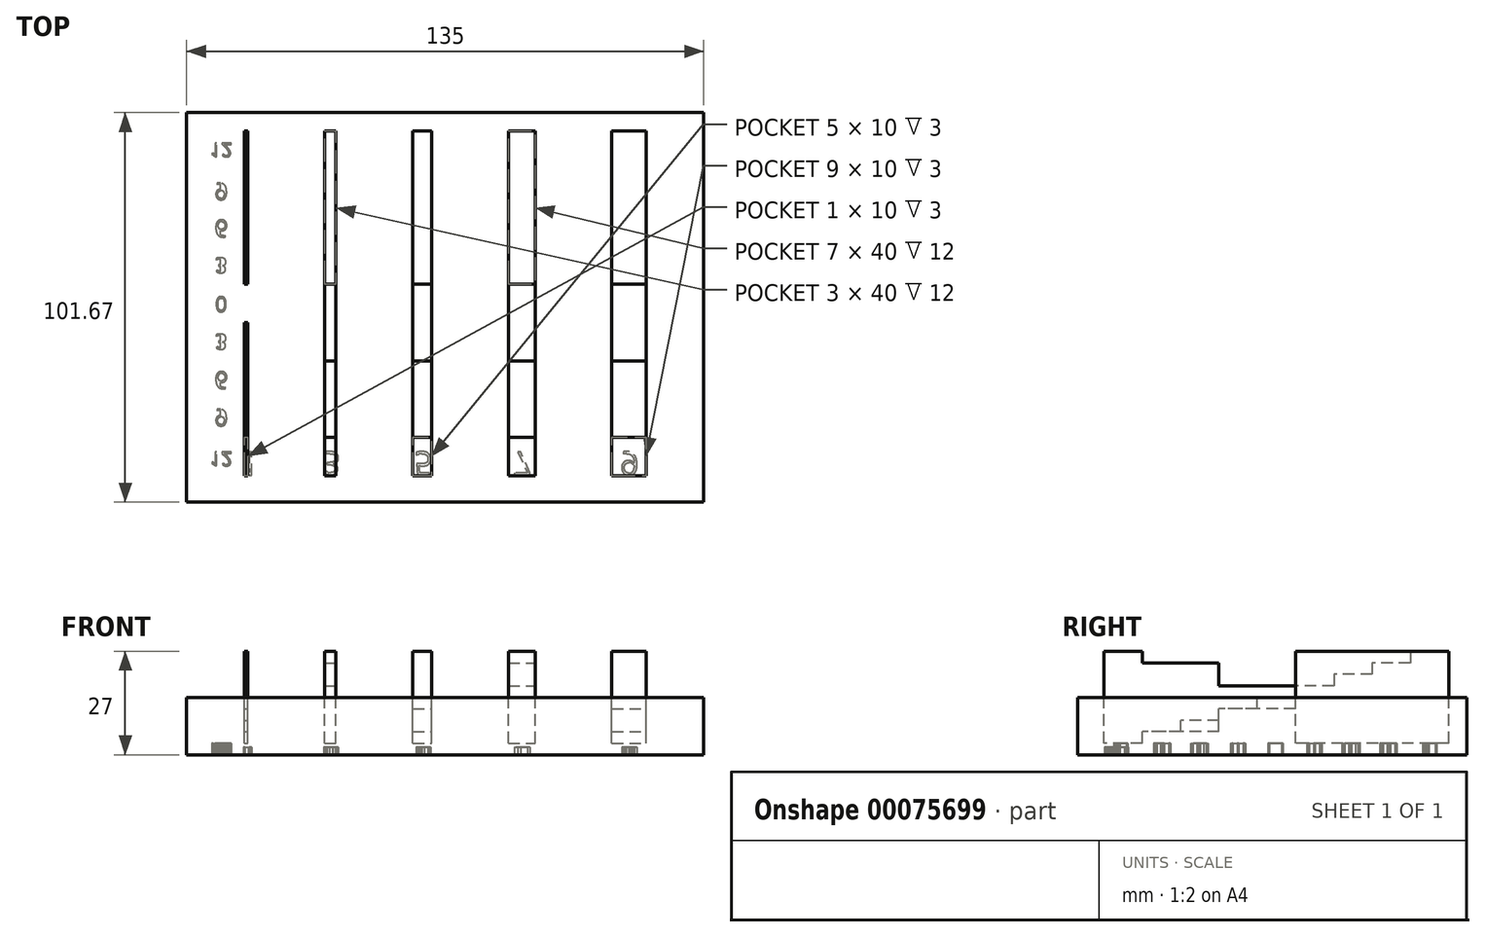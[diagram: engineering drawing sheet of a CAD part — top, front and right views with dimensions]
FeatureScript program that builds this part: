
annotation { "Feature Type Name" : "Feature", "Feature Type Description" : "" }
export const myFeature = defineFeature(function(context is Context, id is Id, definition is map)
    precondition{}
    {
        {
            var Q0;
            Q0=qCreatedBy(makeId("Top.planeOp"),FACE);
            var sketch = newSketch(context, id + "F0", { "sketchPlane" : qUnion([Q0])});
            skLineSegment(sketch, "E0.bottom", {"start": v(-38.42, 41.06) * mm, "end": v(-37.42, 41.06) * mm});
            skLineSegment(sketch, "E0.top", {"start": v(-38.42, 31.06) * mm, "end": v(-37.42, 31.06) * mm});
            skLineSegment(sketch, "E0.left", {"start": v(-38.42, 41.06) * mm, "end": v(-38.42, 31.06) * mm});
            skLineSegment(sketch, "E0.right", {"start": v(-37.42, 41.06) * mm, "end": v(-37.42, 31.06) * mm});
            skLineSegment(sketch, "E1.top", {"start": v(-38.42, 21.06) * mm, "end": v(-37.42, 21.06) * mm});
            skLineSegment(sketch, "E1.left", {"start": v(-38.42, 31.06) * mm, "end": v(-38.42, 21.06) * mm});
            skLineSegment(sketch, "E1.right", {"start": v(-37.42, 31.06) * mm, "end": v(-37.42, 21.06) * mm});
            skLineSegment(sketch, "E2.top", {"start": v(-38.42, 11.06) * mm, "end": v(-37.42, 11.06) * mm});
            skLineSegment(sketch, "E2.left", {"start": v(-38.42, 21.06) * mm, "end": v(-38.42, 11.06) * mm});
            skLineSegment(sketch, "E2.right", {"start": v(-37.42, 21.06) * mm, "end": v(-37.42, 11.06) * mm});
            skLineSegment(sketch, "E3.top", {"start": v(-38.42, 1.06) * mm, "end": v(-37.42, 1.06) * mm});
            skLineSegment(sketch, "E3.left", {"start": v(-38.42, 11.06) * mm, "end": v(-38.42, 1.06) * mm});
            skLineSegment(sketch, "E3.right", {"start": v(-37.42, 11.06) * mm, "end": v(-37.42, 1.06) * mm});
            skLineSegment(sketch, "E4.top", {"start": v(-38.42, -8.94) * mm, "end": v(-37.42, -8.94) * mm});
            skLineSegment(sketch, "E4.left", {"start": v(-38.42, 1.06) * mm, "end": v(-38.42, -8.94) * mm});
            skLineSegment(sketch, "E4.right", {"start": v(-37.42, 1.06) * mm, "end": v(-37.42, -8.94) * mm});
            skLineSegment(sketch, "E5.top", {"start": v(-38.42, -18.94) * mm, "end": v(-37.42, -18.94) * mm});
            skLineSegment(sketch, "E5.left", {"start": v(-38.42, -8.94) * mm, "end": v(-38.42, -18.94) * mm});
            skLineSegment(sketch, "E5.right", {"start": v(-37.42, -8.94) * mm, "end": v(-37.42, -18.94) * mm});
            skLineSegment(sketch, "E6.top", {"start": v(-38.42, -28.94) * mm, "end": v(-37.42, -28.94) * mm});
            skLineSegment(sketch, "E6.left", {"start": v(-38.42, -18.94) * mm, "end": v(-38.42, -28.94) * mm});
            skLineSegment(sketch, "E6.right", {"start": v(-37.42, -18.94) * mm, "end": v(-37.42, -28.94) * mm});
            skLineSegment(sketch, "E7.top", {"start": v(-38.42, -38.94) * mm, "end": v(-37.42, -38.94) * mm});
            skLineSegment(sketch, "E7.left", {"start": v(-38.42, -28.94) * mm, "end": v(-38.42, -38.94) * mm});
            skLineSegment(sketch, "E7.right", {"start": v(-37.42, -28.94) * mm, "end": v(-37.42, -38.94) * mm});
            skLineSegment(sketch, "E8.top", {"start": v(-17.42, -18.94) * mm, "end": v(-14.42, -18.94) * mm});
            skLineSegment(sketch, "E9.bottom", {"start": v(-17.42, -38.94) * mm, "end": v(-14.42, -38.94) * mm});
            skLineSegment(sketch, "E10.right", {"start": v(-14.42, -18.94) * mm, "end": v(-14.42, -28.94) * mm});
            skLineSegment(sketch, "E11.left", {"start": v(-17.42, 21.06) * mm, "end": v(-17.42, 11.06) * mm});
            skLineSegment(sketch, "E10.left", {"start": v(-17.42, -18.94) * mm, "end": v(-17.42, -28.94) * mm});
            skLineSegment(sketch, "E12.bottom", {"start": v(-17.42, 1.06) * mm, "end": v(-14.42, 1.06) * mm});
            skLineSegment(sketch, "E12.right", {"start": v(-14.42, 1.06) * mm, "end": v(-14.42, -8.94) * mm});
            skLineSegment(sketch, "E13.left", {"start": v(-17.42, 11.06) * mm, "end": v(-17.42, 1.06) * mm});
            skLineSegment(sketch, "E13.right", {"start": v(-14.42, 11.06) * mm, "end": v(-14.42, 1.06) * mm});
            skLineSegment(sketch, "E14.left", {"start": v(-17.42, 41.06) * mm, "end": v(-17.42, 31.06) * mm});
            skLineSegment(sketch, "E15.left", {"start": v(-17.42, 31.06) * mm, "end": v(-17.42, 21.06) * mm});
            skLineSegment(sketch, "E15.right", {"start": v(-14.42, 31.06) * mm, "end": v(-14.42, 21.06) * mm});
            skLineSegment(sketch, "E11.right", {"start": v(-14.42, 21.06) * mm, "end": v(-14.42, 11.06) * mm});
            skLineSegment(sketch, "E8.right", {"start": v(-14.42, -8.94) * mm, "end": v(-14.42, -18.94) * mm});
            skLineSegment(sketch, "E16.left", {"start": v(-17.42, -28.94) * mm, "end": v(-17.42, -38.94) * mm});
            skLineSegment(sketch, "E8.left", {"start": v(-17.42, -8.94) * mm, "end": v(-17.42, -18.94) * mm});
            skLineSegment(sketch, "E12.left", {"start": v(-17.42, 1.06) * mm, "end": v(-17.42, -8.94) * mm});
            skLineSegment(sketch, "E16.right", {"start": v(-14.42, -28.94) * mm, "end": v(-14.42, -38.94) * mm});
            skLineSegment(sketch, "E14.bottom", {"start": v(-17.42, 41.06) * mm, "end": v(-14.42, 41.06) * mm});
            skLineSegment(sketch, "E14.right", {"start": v(-14.42, 41.06) * mm, "end": v(-14.42, 31.06) * mm});
            skLineSegment(sketch, "E17.top", {"start": v(5.58, -18.94) * mm, "end": v(10.58, -18.94) * mm});
            skLineSegment(sketch, "E18.bottom", {"start": v(5.58, -38.94) * mm, "end": v(10.58, -38.94) * mm});
            skLineSegment(sketch, "E19.right", {"start": v(10.58, -18.94) * mm, "end": v(10.58, -28.94) * mm});
            skLineSegment(sketch, "E20.left", {"start": v(5.58, 21.06) * mm, "end": v(5.58, 11.06) * mm});
            skLineSegment(sketch, "E19.left", {"start": v(5.58, -18.94) * mm, "end": v(5.58, -28.94) * mm});
            skLineSegment(sketch, "E21.bottom", {"start": v(5.58, 1.06) * mm, "end": v(10.58, 1.06) * mm});
            skLineSegment(sketch, "E21.right", {"start": v(10.58, 1.06) * mm, "end": v(10.58, -8.94) * mm});
            skLineSegment(sketch, "E22.left", {"start": v(5.58, 11.06) * mm, "end": v(5.58, 1.06) * mm});
            skLineSegment(sketch, "E22.right", {"start": v(10.58, 11.06) * mm, "end": v(10.58, 1.06) * mm});
            skLineSegment(sketch, "E23.left", {"start": v(5.58, 41.06) * mm, "end": v(5.58, 31.06) * mm});
            skLineSegment(sketch, "E24.left", {"start": v(5.58, 31.06) * mm, "end": v(5.58, 21.06) * mm});
            skLineSegment(sketch, "E24.right", {"start": v(10.58, 31.06) * mm, "end": v(10.58, 21.06) * mm});
            skLineSegment(sketch, "E20.right", {"start": v(10.58, 21.06) * mm, "end": v(10.58, 11.06) * mm});
            skLineSegment(sketch, "E17.right", {"start": v(10.58, -8.94) * mm, "end": v(10.58, -18.94) * mm});
            skLineSegment(sketch, "E25.left", {"start": v(5.58, -28.94) * mm, "end": v(5.58, -38.94) * mm});
            skLineSegment(sketch, "E17.left", {"start": v(5.58, -8.94) * mm, "end": v(5.58, -18.94) * mm});
            skLineSegment(sketch, "E21.left", {"start": v(5.58, 1.06) * mm, "end": v(5.58, -8.94) * mm});
            skLineSegment(sketch, "E25.right", {"start": v(10.58, -28.94) * mm, "end": v(10.58, -38.94) * mm});
            skLineSegment(sketch, "E23.bottom", {"start": v(5.58, 41.06) * mm, "end": v(10.58, 41.06) * mm});
            skLineSegment(sketch, "E23.right", {"start": v(10.58, 41.06) * mm, "end": v(10.58, 31.06) * mm});
            skLineSegment(sketch, "E26.top", {"start": v(30.58, -18.94) * mm, "end": v(37.58, -18.94) * mm});
            skLineSegment(sketch, "E27.bottom", {"start": v(30.58, -38.94) * mm, "end": v(37.58, -38.94) * mm});
            skLineSegment(sketch, "E28.right", {"start": v(37.58, -18.94) * mm, "end": v(37.58, -28.94) * mm});
            skLineSegment(sketch, "E29.left", {"start": v(30.58, 21.06) * mm, "end": v(30.58, 11.06) * mm});
            skLineSegment(sketch, "E28.left", {"start": v(30.58, -18.94) * mm, "end": v(30.58, -28.94) * mm});
            skLineSegment(sketch, "E30.bottom", {"start": v(30.58, 1.06) * mm, "end": v(37.58, 1.06) * mm});
            skLineSegment(sketch, "E30.right", {"start": v(37.58, 1.06) * mm, "end": v(37.58, -8.94) * mm});
            skLineSegment(sketch, "E31.left", {"start": v(30.58, 11.06) * mm, "end": v(30.58, 1.06) * mm});
            skLineSegment(sketch, "E31.right", {"start": v(37.58, 11.06) * mm, "end": v(37.58, 1.06) * mm});
            skLineSegment(sketch, "E32.left", {"start": v(30.58, 41.06) * mm, "end": v(30.58, 31.06) * mm});
            skLineSegment(sketch, "E33.left", {"start": v(30.58, 31.06) * mm, "end": v(30.58, 21.06) * mm});
            skLineSegment(sketch, "E33.right", {"start": v(37.58, 31.06) * mm, "end": v(37.58, 21.06) * mm});
            skLineSegment(sketch, "E29.right", {"start": v(37.58, 21.06) * mm, "end": v(37.58, 11.06) * mm});
            skLineSegment(sketch, "E26.right", {"start": v(37.58, -8.94) * mm, "end": v(37.58, -18.94) * mm});
            skLineSegment(sketch, "E34.left", {"start": v(30.58, -28.94) * mm, "end": v(30.58, -38.94) * mm});
            skLineSegment(sketch, "E26.left", {"start": v(30.58, -8.94) * mm, "end": v(30.58, -18.94) * mm});
            skLineSegment(sketch, "E30.left", {"start": v(30.58, 1.06) * mm, "end": v(30.58, -8.94) * mm});
            skLineSegment(sketch, "E34.right", {"start": v(37.58, -28.94) * mm, "end": v(37.58, -38.94) * mm});
            skLineSegment(sketch, "E32.bottom", {"start": v(30.58, 41.06) * mm, "end": v(37.58, 41.06) * mm});
            skLineSegment(sketch, "E32.right", {"start": v(37.58, 41.06) * mm, "end": v(37.58, 31.06) * mm});
            skLineSegment(sketch, "E35.top", {"start": v(57.58, -18.94) * mm, "end": v(66.58, -18.94) * mm});
            skLineSegment(sketch, "E36.bottom", {"start": v(57.58, -38.94) * mm, "end": v(66.58, -38.94) * mm});
            skLineSegment(sketch, "E37.right", {"start": v(66.58, -18.94) * mm, "end": v(66.58, -28.94) * mm});
            skLineSegment(sketch, "E38.left", {"start": v(57.58, 21.06) * mm, "end": v(57.58, 11.06) * mm});
            skLineSegment(sketch, "E37.left", {"start": v(57.58, -18.94) * mm, "end": v(57.58, -28.94) * mm});
            skLineSegment(sketch, "E39.bottom", {"start": v(57.58, 1.06) * mm, "end": v(66.58, 1.06) * mm});
            skLineSegment(sketch, "E39.right", {"start": v(66.58, 1.06) * mm, "end": v(66.58, -8.94) * mm});
            skLineSegment(sketch, "E40.left", {"start": v(57.58, 11.06) * mm, "end": v(57.58, 1.06) * mm});
            skLineSegment(sketch, "E40.right", {"start": v(66.58, 11.06) * mm, "end": v(66.58, 1.06) * mm});
            skLineSegment(sketch, "E41.left", {"start": v(57.58, 41.06) * mm, "end": v(57.58, 31.06) * mm});
            skLineSegment(sketch, "E42.left", {"start": v(57.58, 31.06) * mm, "end": v(57.58, 21.06) * mm});
            skLineSegment(sketch, "E42.right", {"start": v(66.58, 31.06) * mm, "end": v(66.58, 21.06) * mm});
            skLineSegment(sketch, "E38.right", {"start": v(66.58, 21.06) * mm, "end": v(66.58, 11.06) * mm});
            skLineSegment(sketch, "E35.right", {"start": v(66.58, -8.94) * mm, "end": v(66.58, -18.94) * mm});
            skLineSegment(sketch, "E43.left", {"start": v(57.58, -28.94) * mm, "end": v(57.58, -38.94) * mm});
            skLineSegment(sketch, "E35.left", {"start": v(57.58, -8.94) * mm, "end": v(57.58, -18.94) * mm});
            skLineSegment(sketch, "E39.left", {"start": v(57.58, 1.06) * mm, "end": v(57.58, -8.94) * mm});
            skLineSegment(sketch, "E43.right", {"start": v(66.58, -28.94) * mm, "end": v(66.58, -38.94) * mm});
            skLineSegment(sketch, "E41.bottom", {"start": v(57.58, 41.06) * mm, "end": v(66.58, 41.06) * mm});
            skLineSegment(sketch, "E41.right", {"start": v(66.58, 41.06) * mm, "end": v(66.58, 31.06) * mm});
            skLineSegment(sketch, "E44.bottom", {"start": v(-53.42, 45.85) * mm, "end": v(81.58, 45.85) * mm});
            skLineSegment(sketch, "E44.top", {"start": v(-53.42, -55.82) * mm, "end": v(81.58, -55.82) * mm});
            skLineSegment(sketch, "E44.left", {"start": v(-53.42, 45.85) * mm, "end": v(-53.42, -55.82) * mm});
            skLineSegment(sketch, "E44.right", {"start": v(81.58, 45.85) * mm, "end": v(81.58, -55.82) * mm});
            skLineSegment(sketch, "E45", {"start": v(-14.42, 1.06) * mm, "end": v(5.58, 1.06) * mm});
            skLineSegment(sketch, "E46", {"start": v(10.58, 1.06) * mm, "end": v(30.58, 1.06) * mm});
            skLineSegment(sketch, "E47", {"start": v(37.58, 1.06) * mm, "end": v(57.58, 1.06) * mm});
            skLineSegment(sketch, "E48", {"start": v(66.58, 1.06) * mm, "end": v(81.58, 1.06) * mm});
            skLineSegment(sketch, "E49", {"start": v(-38.42, 1.06) * mm, "end": v(-53.42, 1.06) * mm});
            skLineSegment(sketch, "E50", {"start": v(-37.42, 1.06) * mm, "end": v(-17.42, 1.06) * mm});
            skLineSegment(sketch, "E51", {"start": v(-38.42, -38.94) * mm, "end": v(-38.42, -48.94) * mm});
            skLineSegment(sketch, "E52", {"start": v(-38.42, -48.94) * mm, "end": v(-37.42, -48.94) * mm});
            skLineSegment(sketch, "E53", {"start": v(-37.42, -48.94) * mm, "end": v(-37.42, -38.94) * mm});
            skLineSegment(sketch, "E54", {"start": v(-17.42, -38.94) * mm, "end": v(-17.42, -48.94) * mm});
            skLineSegment(sketch, "E55", {"start": v(-17.42, -48.94) * mm, "end": v(-14.42, -48.94) * mm});
            skLineSegment(sketch, "E56", {"start": v(-14.42, -48.94) * mm, "end": v(-14.42, -38.94) * mm});
            skLineSegment(sketch, "E57", {"start": v(5.58, -38.94) * mm, "end": v(5.58, -48.94) * mm});
            skLineSegment(sketch, "E58", {"start": v(5.58, -48.94) * mm, "end": v(10.58, -48.94) * mm});
            skLineSegment(sketch, "E59", {"start": v(10.58, -48.94) * mm, "end": v(10.58, -38.94) * mm});
            skLineSegment(sketch, "E60", {"start": v(30.58, -38.94) * mm, "end": v(30.58, -48.94) * mm});
            skLineSegment(sketch, "E61", {"start": v(30.58, -48.94) * mm, "end": v(37.58, -48.94) * mm});
            skLineSegment(sketch, "E62", {"start": v(37.58, -48.94) * mm, "end": v(37.58, -38.94) * mm});
            skLineSegment(sketch, "E63", {"start": v(57.58, -38.94) * mm, "end": v(57.58, -48.94) * mm});
            skLineSegment(sketch, "E64", {"start": v(57.58, -48.94) * mm, "end": v(66.58, -48.94) * mm});
            skLineSegment(sketch, "E65", {"start": v(66.58, -48.94) * mm, "end": v(66.58, -38.94) * mm});
            skSolve(sketch);
        }
        {
            var Q0;
            Q0=makeQuery(id+"F0.imprint","IMPRINT",FACE,{"disambiguationData":[TD([[makeQuery(id+"F0.imprint","IMPRINT",EDGE,{"derivedFrom":sQuery(id+"F0.wireOp",EDGE,"E27.right")}),-1.0]])]});
            var Q1;
            Q1=makeQuery(id+"F0.imprint","IMPRINT",FACE,{"disambiguationData":[TD([[makeQuery(id+"F0.imprint","IMPRINT",EDGE,{"derivedFrom":sQuery(id+"F0.wireOp",EDGE,"E9.right")}),-1.0]])]});
            var Q2;
            Q2=makeQuery(id+"F0.imprint","IMPRINT",FACE,{"disambiguationData":[TD([[makeQuery(id+"F0.imprint","IMPRINT",EDGE,{"derivedFrom":sQuery(id+"F0.wireOp",EDGE,"E36.right")}),-1.0]])]});
            var Q3;
            Q3=makeQuery(id+"F0.imprint","IMPRINT",FACE,{"disambiguationData":[TD([[makeQuery(id+"F0.imprint","IMPRINT",EDGE,{"derivedFrom":sQuery(id+"F0.wireOp",EDGE,"E18.right")}),-1.0]])]});
            var Q4;
            Q4=makeQuery(id+"F0.imprint","IMPRINT",FACE,{"disambiguationData":[TD([[makeQuery(id+"F0.imprint","IMPRINT",EDGE,{"derivedFrom":sQuery(id+"F0.wireOp",EDGE,"E22.left")}),1.0]])]});
            var Q5;
            Q5=makeQuery(id+"F0.imprint","IMPRINT",FACE,{"disambiguationData":[TD([[makeQuery(id+"F0.imprint","IMPRINT",EDGE,{"derivedFrom":sQuery(id+"F0.wireOp",EDGE,"E40.left")}),1.0]])]});
            var Q6;
            Q6=makeQuery(id+"F0.imprint","IMPRINT",FACE,{"disambiguationData":[TD([[makeQuery(id+"F0.imprint","IMPRINT",EDGE,{"derivedFrom":sQuery(id+"F0.wireOp",EDGE,"E16.left")}),1.0]])]});
            var Q7;
            Q7=makeQuery(id+"F0.imprint","IMPRINT",FACE,{"disambiguationData":[TD([[makeQuery(id+"F0.imprint","IMPRINT",EDGE,{"derivedFrom":sQuery(id+"F0.wireOp",EDGE,"E19.right")}),-1.0]])]});
            var Q8;
            Q8=makeQuery(id+"F0.imprint","IMPRINT",FACE,{"disambiguationData":[TD([[makeQuery(id+"F0.imprint","IMPRINT",EDGE,{"derivedFrom":sQuery(id+"F0.wireOp",EDGE,"E37.right")}),-1.0]])]});
            var Q9;
            Q9=makeQuery(id+"F0.imprint","IMPRINT",FACE,{"disambiguationData":[TD([[makeQuery(id+"F0.imprint","IMPRINT",EDGE,{"derivedFrom":sQuery(id+"F0.wireOp",EDGE,"E38.left")}),1.0]])]});
            var Q10;
            {var subQ0=sQuery(id+"F0.wireOp",EDGE,"E20.left");Q10=makeQuery(id+"F0.imprint","IMPRINT",FACE,{"disambiguationData":[TD([[makeQuery(id+"F0.imprint","IMPRINT",EDGE,{"derivedFrom":subQ0}),1.0]])]});}
            var Q11;
            Q11=makeQuery(id+"F0.imprint","IMPRINT",FACE,{"disambiguationData":[TD([[makeQuery(id+"F0.imprint","IMPRINT",EDGE,{"derivedFrom":sQuery(id+"F0.wireOp",EDGE,"E39.right")}),-1.0]])]});
            var Q12;
            Q12=makeQuery(id+"F0.imprint","IMPRINT",FACE,{"disambiguationData":[TD([[makeQuery(id+"F0.imprint","IMPRINT",EDGE,{"derivedFrom":sQuery(id+"F0.wireOp",EDGE,"E21.right")}),-1.0]])]});
            var Q13;
            Q13=makeQuery(id+"F0.imprint","IMPRINT",FACE,{"disambiguationData":[TD([[makeQuery(id+"F0.imprint","IMPRINT",EDGE,{"derivedFrom":sQuery(id+"F0.wireOp",EDGE,"E10.right")}),-1.0]])]});
            var Q14;
            Q14=makeQuery(id+"F0.imprint","IMPRINT",FACE,{"disambiguationData":[TD([[makeQuery(id+"F0.imprint","IMPRINT",EDGE,{"derivedFrom":sQuery(id+"F0.wireOp",EDGE,"E28.right")}),-1.0]])]});
            var Q15;
            {var subQ0=sQuery(id+"F0.wireOp",EDGE,"E11.left");Q15=makeQuery(id+"F0.imprint","IMPRINT",FACE,{"disambiguationData":[TD([[makeQuery(id+"F0.imprint","IMPRINT",EDGE,{"derivedFrom":subQ0}),1.0]])]});}
            var Q16;
            Q16=makeQuery(id+"F0.imprint","IMPRINT",FACE,{"disambiguationData":[TD([[makeQuery(id+"F0.imprint","IMPRINT",EDGE,{"derivedFrom":sQuery(id+"F0.wireOp",EDGE,"E35.right")}),-1.0]])]});
            var Q17;
            Q17=makeQuery(id+"F0.imprint","IMPRINT",FACE,{"disambiguationData":[TD([[makeQuery(id+"F0.imprint","IMPRINT",EDGE,{"derivedFrom":sQuery(id+"F0.wireOp",EDGE,"E17.right")}),-1.0]])]});
            var Q18;
            {var subQ0=sQuery(id+"F0.wireOp",EDGE,"E29.left");Q18=makeQuery(id+"F0.imprint","IMPRINT",FACE,{"disambiguationData":[TD([[makeQuery(id+"F0.imprint","IMPRINT",EDGE,{"derivedFrom":subQ0}),1.0]])]});}
            var Q19;
            {var subQ0=sQuery(id+"F0.wireOp",EDGE,"E24.left");Q19=makeQuery(id+"F0.imprint","IMPRINT",FACE,{"disambiguationData":[TD([[makeQuery(id+"F0.imprint","IMPRINT",EDGE,{"derivedFrom":subQ0}),1.0]])]});}
            var Q20;
            Q20=makeQuery(id+"F0.imprint","IMPRINT",FACE,{"disambiguationData":[TD([[makeQuery(id+"F0.imprint","IMPRINT",EDGE,{"derivedFrom":sQuery(id+"F0.wireOp",EDGE,"E43.left")}),1.0]])]});
            var Q21;
            Q21=makeQuery(id+"F0.imprint","IMPRINT",FACE,{"disambiguationData":[TD([[makeQuery(id+"F0.imprint","IMPRINT",EDGE,{"derivedFrom":sQuery(id+"F0.wireOp",EDGE,"E25.left")}),1.0]])]});
            var Q22;
            Q22=makeQuery(id+"F0.imprint","IMPRINT",FACE,{"disambiguationData":[TD([[makeQuery(id+"F0.imprint","IMPRINT",EDGE,{"derivedFrom":sQuery(id+"F0.wireOp",EDGE,"E34.left")}),1.0]])]});
            var Q23;
            Q23=makeQuery(id+"F0.imprint","IMPRINT",FACE,{"disambiguationData":[TD([[makeQuery(id+"F0.imprint","IMPRINT",EDGE,{"derivedFrom":sQuery(id+"F0.wireOp",EDGE,"E12.right")}),-1.0]])]});
            var Q24;
            Q24=makeQuery(id+"F0.imprint","IMPRINT",FACE,{"disambiguationData":[TD([[makeQuery(id+"F0.imprint","IMPRINT",EDGE,{"derivedFrom":sQuery(id+"F0.wireOp",EDGE,"E30.right")}),-1.0]])]});
            var Q25;
            {var subQ0=sQuery(id+"F0.wireOp",EDGE,"E31.left");Q25=makeQuery(id+"F0.imprint","IMPRINT",FACE,{"disambiguationData":[TD([[makeQuery(id+"F0.imprint","IMPRINT",EDGE,{"derivedFrom":subQ0}),1.0]])]});}
            var Q26;
            {var subQ0=sQuery(id+"F0.wireOp",EDGE,"E13.left");Q26=makeQuery(id+"F0.imprint","IMPRINT",FACE,{"disambiguationData":[TD([[makeQuery(id+"F0.imprint","IMPRINT",EDGE,{"derivedFrom":subQ0}),1.0]])]});}
            var Q27;
            Q27=makeQuery(id+"F0.imprint","IMPRINT",FACE,{"disambiguationData":[TD([[makeQuery(id+"F0.imprint","IMPRINT",EDGE,{"derivedFrom":sQuery(id+"F0.wireOp",EDGE,"2a3499dd-0f45-481c-83e2-7a4d8ce4059a.right")}),-1.0]])]});
            var Q28;
            Q28=makeQuery(id+"F0.imprint","IMPRINT",FACE,{"disambiguationData":[TD([[makeQuery(id+"F0.imprint","IMPRINT",EDGE,{"derivedFrom":sQuery(id+"F0.wireOp",EDGE,"b8b1e6fe-e81b-4528-8c0a-a502875816c5.right")}),-1.0]])]});
            var Q29;
            Q29=makeQuery(id+"F0.imprint","IMPRINT",FACE,{"disambiguationData":[TD([[makeQuery(id+"F0.imprint","IMPRINT",EDGE,{"derivedFrom":sQuery(id+"F0.wireOp",EDGE,"E23.left")}),1.0]])]});
            var Q30;
            Q30=makeQuery(id+"F0.imprint","IMPRINT",FACE,{"disambiguationData":[TD([[makeQuery(id+"F0.imprint","IMPRINT",EDGE,{"derivedFrom":sQuery(id+"F0.wireOp",EDGE,"b7528009-93d2-41cc-b916-c0be01132167.right")}),-1.0]])]});
            var Q31;
            Q31=makeQuery(id+"F0.imprint","IMPRINT",FACE,{"disambiguationData":[TD([[makeQuery(id+"F0.imprint","IMPRINT",EDGE,{"derivedFrom":sQuery(id+"F0.wireOp",EDGE,"cfbb6618-f7cc-4c27-93e8-6fec4e00b0a7.right")}),-1.0]])]});
            var Q32;
            Q32=makeQuery(id+"F0.imprint","IMPRINT",FACE,{"disambiguationData":[TD([[makeQuery(id+"F0.imprint","IMPRINT",EDGE,{"derivedFrom":sQuery(id+"F0.wireOp",EDGE,"E33.left")}),1.0]])]});
            var Q33;
            Q33=makeQuery(id+"F0.imprint","IMPRINT",FACE,{"disambiguationData":[TD([[makeQuery(id+"F0.imprint","IMPRINT",EDGE,{"derivedFrom":sQuery(id+"F0.wireOp",EDGE,"E15.left")}),1.0]])]});
            var Q34;
            Q34=makeQuery(id+"F0.imprint","IMPRINT",FACE,{"disambiguationData":[TD([[makeQuery(id+"F0.imprint","IMPRINT",EDGE,{"derivedFrom":sQuery(id+"F0.wireOp",EDGE,"E26.right")}),-1.0]])]});
            var Q35;
            Q35=makeQuery(id+"F0.imprint","IMPRINT",FACE,{"disambiguationData":[TD([[makeQuery(id+"F0.imprint","IMPRINT",EDGE,{"derivedFrom":sQuery(id+"F0.wireOp",EDGE,"E8.right")}),-1.0]])]});
            var Q36;
            Q36=makeQuery(id+"F0.imprint","IMPRINT",FACE,{"disambiguationData":[TD([[makeQuery(id+"F0.imprint","IMPRINT",EDGE,{"derivedFrom":sQuery(id+"F0.wireOp",EDGE,"E42.left")}),1.0]])]});
            var Q37;
            Q37=makeQuery(id+"F0.imprint","IMPRINT",FACE,{"disambiguationData":[TD([[makeQuery(id+"F0.imprint","IMPRINT",EDGE,{"derivedFrom":sQuery(id+"F0.wireOp",EDGE,"E6.top")}),-1.0]])]});
            var Q38;
            Q38=makeQuery(id+"F0.imprint","IMPRINT",FACE,{"disambiguationData":[TD([[makeQuery(id+"F0.imprint","IMPRINT",EDGE,{"derivedFrom":sQuery(id+"F0.wireOp",EDGE,"E5.top")}),-1.0]])]});
            var Q39;
            Q39=makeQuery(id+"F0.imprint","IMPRINT",FACE,{"disambiguationData":[TD([[makeQuery(id+"F0.imprint","IMPRINT",EDGE,{"derivedFrom":sQuery(id+"F0.wireOp",EDGE,"E3.top")}),-1.0]])]});
            var Q40;
            Q40=makeQuery(id+"F0.imprint","IMPRINT",FACE,{"disambiguationData":[TD([[makeQuery(id+"F0.imprint","IMPRINT",EDGE,{"derivedFrom":sQuery(id+"F0.wireOp",EDGE,"E4.top")}),-1.0]])]});
            var Q41;
            Q41=makeQuery(id+"F0.imprint","IMPRINT",FACE,{"disambiguationData":[TD([[makeQuery(id+"F0.imprint","IMPRINT",EDGE,{"derivedFrom":sQuery(id+"F0.wireOp",EDGE,"7e96f1e9-1112-4445-a7ef-e244a0d670a8.bottom")}),-1.0]])]});
            var Q42;
            Q42=makeQuery(id+"F0.imprint","IMPRINT",FACE,{"disambiguationData":[TD([[makeQuery(id+"F0.imprint","IMPRINT",EDGE,{"derivedFrom":sQuery(id+"F0.wireOp",EDGE,"E14.left")}),1.0]])]});
            var Q43;
            Q43=makeQuery(id+"F0.imprint","IMPRINT",FACE,{"disambiguationData":[TD([[makeQuery(id+"F0.imprint","IMPRINT",EDGE,{"derivedFrom":sQuery(id+"F0.wireOp",EDGE,"E0.top")}),-1.0]])]});
            var Q44;
            {var subQ0=sQuery(id+"F0.wireOp",EDGE,"E2.left");Q44=makeQuery(id+"F0.imprint","IMPRINT",FACE,{"disambiguationData":[TD([[makeQuery(id+"F0.imprint","IMPRINT",EDGE,{"derivedFrom":subQ0}),1.0]])]});}
            var Q45;
            Q45=makeQuery(id+"F0.imprint","IMPRINT",FACE,{"disambiguationData":[TD([[makeQuery(id+"F0.imprint","IMPRINT",EDGE,{"derivedFrom":sQuery(id+"F0.wireOp",EDGE,"E2.top")}),-1.0]])]});
            var Q46;
            Q46=makeQuery(id+"F0.imprint","IMPRINT",FACE,{"disambiguationData":[TD([[makeQuery(id+"F0.imprint","IMPRINT",EDGE,{"derivedFrom":sQuery(id+"F0.wireOp",EDGE,"E0.bottom")}),-1.0]])]});
            var Q47;
            Q47=makeQuery(id+"F0.imprint","IMPRINT",FACE,{"disambiguationData":[TD([[makeQuery(id+"F0.imprint","IMPRINT",EDGE,{"derivedFrom":sQuery(id+"F0.wireOp",EDGE,"E41.left")}),1.0]])]});
            var Q48;
            Q48=makeQuery(id+"F0.imprint","IMPRINT",FACE,{"disambiguationData":[TD([[makeQuery(id+"F0.imprint","IMPRINT",EDGE,{"derivedFrom":sQuery(id+"F0.wireOp",EDGE,"E32.left")}),1.0]])]});
            var Q49;
            Q49=makeQuery(id+"F0.imprint","IMPRINT",FACE,{"disambiguationData":[TD([[makeQuery(id+"F0.imprint","IMPRINT",EDGE,{"derivedFrom":sQuery(id+"F0.wireOp",EDGE,"E0.bottom")}),1.0]])]});
            var Q50;
            Q50=makeQuery(id+"F0.imprint","IMPRINT",FACE,{"disambiguationData":[TD([[makeQuery(id+"F0.imprint","IMPRINT",EDGE,{"derivedFrom":sQuery(id+"F0.wireOp",EDGE,"E4.left")}),-1.0]])]});
            var Q51;
            Q51=makeQuery(id+"F0.imprint","IMPRINT",FACE,{"disambiguationData":[TD([[makeQuery(id+"F0.imprint","IMPRINT",EDGE,{"derivedFrom":sQuery(id+"F0.wireOp",EDGE,"E9.bottom")}),-1.0]])]});
            var Q52;
            Q52=makeQuery(id+"F0.imprint","IMPRINT",FACE,{"disambiguationData":[TD([[makeQuery(id+"F0.imprint","IMPRINT",EDGE,{"derivedFrom":sQuery(id+"F0.wireOp",EDGE,"E18.bottom")}),-1.0]])]});
            var Q53;
            Q53=makeQuery(id+"F0.imprint","IMPRINT",FACE,{"disambiguationData":[TD([[makeQuery(id+"F0.imprint","IMPRINT",EDGE,{"derivedFrom":sQuery(id+"F0.wireOp",EDGE,"E27.bottom")}),-1.0]])]});
            var Q54;
            {var subQ0=sQuery(id+"F0.wireOp",EDGE,"E63");Q54=makeQuery(id+"F0.imprint","IMPRINT",FACE,{"disambiguationData":[TD([[makeQuery(id+"F0.imprint","IMPRINT",EDGE,{"derivedFrom":subQ0}),1.0]])]});}
            var Q55;
            Q55=makeQuery(id+"F0.imprint","IMPRINT",FACE,{"disambiguationData":[TD([[makeQuery(id+"F0.imprint","IMPRINT",EDGE,{"derivedFrom":sQuery(id+"F0.wireOp",EDGE,"4589171d-1b87-4397-bdab-a4b340034bb1.bottom")}),-1.0]])]});
            var Q56;
            Q56=makeQuery(id+"F0.imprint","IMPRINT",FACE,{"disambiguationData":[TD([[makeQuery(id+"F0.imprint","IMPRINT",EDGE,{"derivedFrom":sQuery(id+"F0.wireOp",EDGE,"E7.top")}),-1.0]])]});
            extrude(context, id + "F1", {"entities" : qUnion([Q0, Q1, Q2, Q3, Q4, Q5, Q6, Q7, Q8, Q9, Q10, Q11, Q12, Q13, Q14, Q15, Q16, Q17, Q18, Q19, Q20, Q21, Q22, Q23, Q24, Q25, Q26, Q27, Q28, Q29, Q30, Q31, Q32, Q33, Q34, Q35, Q36, Q37, Q38, Q39, Q40, Q41, Q42, Q43, Q44, Q45, Q46, Q47, Q48, Q49, Q50, Q51, Q52, Q53, Q54, Q55, Q56]), "oppositeDirection" : true, "depth" : 15 * mm});
        }
        {
            var Q0;
            Q0=makeQuery(id+"F0.imprint","IMPRINT",FACE,{"disambiguationData":[TD([[makeQuery(id+"F0.imprint","IMPRINT",EDGE,{"derivedFrom":sQuery(id+"F0.wireOp",EDGE,"E41.left")}),1.0]])]});
            var Q1;
            Q1=makeQuery(id+"F0.imprint","IMPRINT",FACE,{"disambiguationData":[TD([[makeQuery(id+"F0.imprint","IMPRINT",EDGE,{"derivedFrom":sQuery(id+"F0.wireOp",EDGE,"E23.left")}),1.0]])]});
            var Q2;
            Q2=makeQuery(id+"F0.imprint","IMPRINT",FACE,{"disambiguationData":[TD([[makeQuery(id+"F0.imprint","IMPRINT",EDGE,{"derivedFrom":sQuery(id+"F0.wireOp",EDGE,"E0.bottom")}),-1.0]])]});
            extrude(context, id + "F2", {"entities" : qUnion([Q0, Q1, Q2]), "operationType" : NewBodyOperationType.ADD, "depth" : 12 * mm});
        }
        {
            var Q0;
            Q0=makeQuery(id+"F0.imprint","IMPRINT",FACE,{"disambiguationData":[TD([[makeQuery(id+"F0.imprint","IMPRINT",EDGE,{"derivedFrom":sQuery(id+"F0.wireOp",EDGE,"E42.left")}),1.0]])]});
            var Q1;
            Q1=makeQuery(id+"F0.imprint","IMPRINT",FACE,{"disambiguationData":[TD([[makeQuery(id+"F0.imprint","IMPRINT",EDGE,{"derivedFrom":sQuery(id+"F0.wireOp",EDGE,"E0.top")}),-1.0]])]});
            var Q2;
            Q2=makeQuery(id+"F0.imprint","IMPRINT",FACE,{"disambiguationData":[TD([[makeQuery(id+"F0.imprint","IMPRINT",EDGE,{"derivedFrom":sQuery(id+"F0.wireOp",EDGE,"E24.left")}),1.0]])]});
            extrude(context, id + "F3", {"entities" : qUnion([Q0, Q1, Q2]), "operationType" : NewBodyOperationType.ADD, "depth" : 9 * mm});
        }
        {
            var Q0;
            Q0=makeQuery(id+"F0.imprint","IMPRINT",FACE,{"disambiguationData":[TD([[makeQuery(id+"F0.imprint","IMPRINT",EDGE,{"derivedFrom":sQuery(id+"F0.wireOp",EDGE,"E38.left")}),1.0]])]});
            var Q1;
            {var subQ0=sQuery(id+"F0.wireOp",EDGE,"E2.left");Q1=makeQuery(id+"F0.imprint","IMPRINT",FACE,{"disambiguationData":[TD([[makeQuery(id+"F0.imprint","IMPRINT",EDGE,{"derivedFrom":subQ0}),1.0]])]});}
            var Q2;
            Q2=makeQuery(id+"F0.imprint","IMPRINT",FACE,{"disambiguationData":[TD([[makeQuery(id+"F0.imprint","IMPRINT",EDGE,{"derivedFrom":sQuery(id+"F0.wireOp",EDGE,"E20.left")}),1.0]])]});
            extrude(context, id + "F4", {"entities" : qUnion([Q0, Q1, Q2]), "operationType" : NewBodyOperationType.ADD, "depth" : 6 * mm});
        }
        {
            var Q0;
            Q0=makeQuery(id+"F0.imprint","IMPRINT",FACE,{"disambiguationData":[TD([[makeQuery(id+"F0.imprint","IMPRINT",EDGE,{"derivedFrom":sQuery(id+"F0.wireOp",EDGE,"E40.left")}),1.0]])]});
            var Q1;
            Q1=makeQuery(id+"F0.imprint","IMPRINT",FACE,{"disambiguationData":[TD([[makeQuery(id+"F0.imprint","IMPRINT",EDGE,{"derivedFrom":sQuery(id+"F0.wireOp",EDGE,"E2.top")}),-1.0]])]});
            var Q2;
            Q2=makeQuery(id+"F0.imprint","IMPRINT",FACE,{"disambiguationData":[TD([[makeQuery(id+"F0.imprint","IMPRINT",EDGE,{"derivedFrom":sQuery(id+"F0.wireOp",EDGE,"E22.left")}),1.0]])]});
            extrude(context, id + "F5", {"entities" : qUnion([Q0, Q1, Q2]), "operationType" : NewBodyOperationType.ADD, "depth" : 3 * mm});
        }
        {
            var Q0;
            Q0=makeQuery(id+"F0.imprint","IMPRINT",FACE,{"disambiguationData":[TD([[makeQuery(id+"F0.imprint","IMPRINT",EDGE,{"derivedFrom":sQuery(id+"F0.wireOp",EDGE,"E35.right")}),-1.0]])]});
            var Q1;
            Q1=makeQuery(id+"F0.imprint","IMPRINT",FACE,{"disambiguationData":[TD([[makeQuery(id+"F0.imprint","IMPRINT",EDGE,{"derivedFrom":sQuery(id+"F0.wireOp",EDGE,"E4.top")}),-1.0]])]});
            var Q2;
            Q2=makeQuery(id+"F0.imprint","IMPRINT",FACE,{"disambiguationData":[TD([[makeQuery(id+"F0.imprint","IMPRINT",EDGE,{"derivedFrom":sQuery(id+"F0.wireOp",EDGE,"E17.right")}),-1.0]])]});
            extrude(context, id + "F6", {"entities" : qUnion([Q0, Q1, Q2]), "operationType" : NewBodyOperationType.REMOVE, "oppositeDirection" : true, "depth" : 3 * mm});
        }
        {
            var Q0;
            Q0=makeQuery(id+"F0.imprint","IMPRINT",FACE,{"disambiguationData":[TD([[makeQuery(id+"F0.imprint","IMPRINT",EDGE,{"derivedFrom":sQuery(id+"F0.wireOp",EDGE,"E37.right")}),-1.0]])]});
            var Q1;
            Q1=makeQuery(id+"F0.imprint","IMPRINT",FACE,{"disambiguationData":[TD([[makeQuery(id+"F0.imprint","IMPRINT",EDGE,{"derivedFrom":sQuery(id+"F0.wireOp",EDGE,"E5.top")}),-1.0]])]});
            var Q2;
            Q2=makeQuery(id+"F0.imprint","IMPRINT",FACE,{"disambiguationData":[TD([[makeQuery(id+"F0.imprint","IMPRINT",EDGE,{"derivedFrom":sQuery(id+"F0.wireOp",EDGE,"E19.right")}),-1.0]])]});
            extrude(context, id + "F7", {"entities" : qUnion([Q0, Q1, Q2]), "operationType" : NewBodyOperationType.REMOVE, "oppositeDirection" : true, "depth" : 6 * mm});
        }
        {
            var Q0;
            Q0=makeQuery(id+"F0.imprint","IMPRINT",FACE,{"disambiguationData":[TD([[makeQuery(id+"F0.imprint","IMPRINT",EDGE,{"derivedFrom":sQuery(id+"F0.wireOp",EDGE,"E43.left")}),1.0]])]});
            var Q1;
            Q1=makeQuery(id+"F0.imprint","IMPRINT",FACE,{"disambiguationData":[TD([[makeQuery(id+"F0.imprint","IMPRINT",EDGE,{"derivedFrom":sQuery(id+"F0.wireOp",EDGE,"E6.top")}),-1.0]])]});
            var Q2;
            Q2=makeQuery(id+"F0.imprint","IMPRINT",FACE,{"disambiguationData":[TD([[makeQuery(id+"F0.imprint","IMPRINT",EDGE,{"derivedFrom":sQuery(id+"F0.wireOp",EDGE,"E25.left")}),1.0]])]});
            extrude(context, id + "F8", {"entities" : qUnion([Q0, Q1, Q2]), "operationType" : NewBodyOperationType.REMOVE, "oppositeDirection" : true, "depth" : 9 * mm});
        }
        {
            var Q0;
            Q0=makeQuery(id+"F0.imprint","IMPRINT",FACE,{"disambiguationData":[TD([[makeQuery(id+"F0.imprint","IMPRINT",EDGE,{"derivedFrom":sQuery(id+"F0.wireOp",EDGE,"4589171d-1b87-4397-bdab-a4b340034bb1.bottom")}),-1.0]])]});
            var Q1;
            Q1=makeQuery(id+"F0.imprint","IMPRINT",FACE,{"disambiguationData":[TD([[makeQuery(id+"F0.imprint","IMPRINT",EDGE,{"derivedFrom":sQuery(id+"F0.wireOp",EDGE,"E18.bottom")}),-1.0]])]});
            var Q2;
            {var subQ0=sQuery(id+"F0.wireOp",EDGE,"E63");Q2=makeQuery(id+"F0.imprint","IMPRINT",FACE,{"disambiguationData":[TD([[makeQuery(id+"F0.imprint","IMPRINT",EDGE,{"derivedFrom":subQ0}),1.0]])]});}
            var Q3;
            Q3=makeQuery(id+"F0.imprint","IMPRINT",FACE,{"disambiguationData":[TD([[makeQuery(id+"F0.imprint","IMPRINT",EDGE,{"derivedFrom":sQuery(id+"F0.wireOp",EDGE,"E7.top")}),-1.0]])]});
            extrude(context, id + "F9", {"entities" : qUnion([Q0, Q1, Q2, Q3]), "operationType" : NewBodyOperationType.REMOVE, "oppositeDirection" : true, "depth" : 12 * mm});
        }
        {
            var Q0;
            Q0=makeQuery(id+"F0.imprint","IMPRINT",FACE,{"disambiguationData":[TD([[makeQuery(id+"F0.imprint","IMPRINT",EDGE,{"derivedFrom":sQuery(id+"F0.wireOp",EDGE,"E14.left")}),1.0]])]});
            var Q1;
            Q1=makeQuery(id+"F0.imprint","IMPRINT",FACE,{"disambiguationData":[TD([[makeQuery(id+"F0.imprint","IMPRINT",EDGE,{"derivedFrom":sQuery(id+"F0.wireOp",EDGE,"E32.left")}),1.0]])]});
            extrude(context, id + "F10", {"entities" : qUnion([Q0, Q1]), "operationType" : NewBodyOperationType.REMOVE, "oppositeDirection" : true, "depth" : 12 * mm});
        }
        {
            var Q0;
            Q0=makeQuery(id+"F0.imprint","IMPRINT",FACE,{"disambiguationData":[TD([[makeQuery(id+"F0.imprint","IMPRINT",EDGE,{"derivedFrom":sQuery(id+"F0.wireOp",EDGE,"E15.left")}),1.0]])]});
            var Q1;
            Q1=makeQuery(id+"F0.imprint","IMPRINT",FACE,{"disambiguationData":[TD([[makeQuery(id+"F0.imprint","IMPRINT",EDGE,{"derivedFrom":sQuery(id+"F0.wireOp",EDGE,"E33.left")}),1.0]])]});
            extrude(context, id + "F11", {"entities" : qUnion([Q0, Q1]), "operationType" : NewBodyOperationType.REMOVE, "oppositeDirection" : true, "depth" : 9 * mm});
        }
        {
            var Q0;
            Q0=makeQuery(id+"F0.imprint","IMPRINT",FACE,{"disambiguationData":[TD([[makeQuery(id+"F0.imprint","IMPRINT",EDGE,{"derivedFrom":sQuery(id+"F0.wireOp",EDGE,"E11.left")}),1.0]])]});
            var Q1;
            Q1=makeQuery(id+"F0.imprint","IMPRINT",FACE,{"disambiguationData":[TD([[makeQuery(id+"F0.imprint","IMPRINT",EDGE,{"derivedFrom":sQuery(id+"F0.wireOp",EDGE,"E29.left")}),1.0]])]});
            extrude(context, id + "F12", {"entities" : qUnion([Q0, Q1]), "operationType" : NewBodyOperationType.REMOVE, "oppositeDirection" : true, "depth" : 6 * mm});
        }
        {
            var Q0;
            Q0=makeQuery(id+"F0.imprint","IMPRINT",FACE,{"disambiguationData":[TD([[makeQuery(id+"F0.imprint","IMPRINT",EDGE,{"derivedFrom":sQuery(id+"F0.wireOp",EDGE,"E13.left")}),1.0]])]});
            var Q1;
            Q1=makeQuery(id+"F0.imprint","IMPRINT",FACE,{"disambiguationData":[TD([[makeQuery(id+"F0.imprint","IMPRINT",EDGE,{"derivedFrom":sQuery(id+"F0.wireOp",EDGE,"E31.left")}),1.0]])]});
            extrude(context, id + "F13", {"entities" : qUnion([Q0, Q1]), "operationType" : NewBodyOperationType.REMOVE, "oppositeDirection" : true, "depth" : 3 * mm});
        }
        {
            var Q0;
            Q0=makeQuery(id+"F0.imprint","IMPRINT",FACE,{"disambiguationData":[TD([[makeQuery(id+"F0.imprint","IMPRINT",EDGE,{"derivedFrom":sQuery(id+"F0.wireOp",EDGE,"E8.right")}),-1.0]])]});
            var Q1;
            Q1=makeQuery(id+"F0.imprint","IMPRINT",FACE,{"disambiguationData":[TD([[makeQuery(id+"F0.imprint","IMPRINT",EDGE,{"derivedFrom":sQuery(id+"F0.wireOp",EDGE,"E26.right")}),-1.0]])]});
            extrude(context, id + "F14", {"entities" : qUnion([Q0, Q1]), "operationType" : NewBodyOperationType.ADD, "depth" : 3 * mm});
        }
        {
            var Q0;
            Q0=makeQuery(id+"F0.imprint","IMPRINT",FACE,{"disambiguationData":[TD([[makeQuery(id+"F0.imprint","IMPRINT",EDGE,{"derivedFrom":sQuery(id+"F0.wireOp",EDGE,"E10.right")}),-1.0]])]});
            var Q1;
            Q1=makeQuery(id+"F0.imprint","IMPRINT",FACE,{"disambiguationData":[TD([[makeQuery(id+"F0.imprint","IMPRINT",EDGE,{"derivedFrom":sQuery(id+"F0.wireOp",EDGE,"E28.right")}),-1.0]])]});
            extrude(context, id + "F15", {"entities" : qUnion([Q0, Q1]), "operationType" : NewBodyOperationType.ADD, "depth" : 6 * mm});
        }
        {
            var Q0;
            Q0=makeQuery(id+"F0.imprint","IMPRINT",FACE,{"disambiguationData":[TD([[makeQuery(id+"F0.imprint","IMPRINT",EDGE,{"derivedFrom":sQuery(id+"F0.wireOp",EDGE,"E16.left")}),1.0]])]});
            var Q1;
            Q1=makeQuery(id+"F0.imprint","IMPRINT",FACE,{"disambiguationData":[TD([[makeQuery(id+"F0.imprint","IMPRINT",EDGE,{"derivedFrom":sQuery(id+"F0.wireOp",EDGE,"E34.left")}),1.0]])]});
            extrude(context, id + "F16", {"entities" : qUnion([Q0, Q1]), "operationType" : NewBodyOperationType.ADD, "depth" : 9 * mm});
        }
        {
            var Q0;
            Q0=makeQuery(id+"F1.opExtrude","CAP_FACE",FACE,{"disambiguationData":[OSD([sQuery(id+"F0.wireOp",EDGE,"E44.bottom"),sQuery(id+"F0.wireOp",EDGE,"E44.top"),sQuery(id+"F0.wireOp",EDGE,"E44.left"),sQuery(id+"F0.wireOp",EDGE,"E44.right")])],"isStart":false});
            var sketch = newSketch(context, id + "F17", { "sketchPlane" : qUnion([Q0])});
            skText(sketch, "E66", { "text": "12", "fontName": "OpenSans-Regular.ttf"});
            skText(sketch, "E67", { "text": "9", "fontName": "OpenSans-Regular.ttf"});
            skText(sketch, "E68", { "text": "6", "fontName": "OpenSans-Regular.ttf"});
            skText(sketch, "E69", { "text": "3", "fontName": "OpenSans-Regular.ttf"});
            skLineSegment(sketch, "E70", {"start": v(-44.56, 55.72) * mm, "end": v(-44.56, -494.01) * mm});
            skText(sketch, "E71", { "text": "3", "fontName": "OpenSans-Regular.ttf"});
            skText(sketch, "E72", { "text": "6", "fontName": "OpenSans-Regular.ttf"});
            skText(sketch, "E73", { "text": "9", "fontName": "OpenSans-Regular.ttf"});
            skText(sketch, "E74", { "text": "12", "fontName": "OpenSans-Regular.ttf"});
            skText(sketch, "E75", { "text": "0", "fontName": "OpenSans-Regular.ttf"});
            const initialGuessF17  = {"E66": [-0.04732, 0.04274, 1, 0, 0.00365], "E67": [-0.04612, 0.0316, 1, 0, 0.00435], "E68": [-0.04617, 0.02182, 1, 0, 0.00443], "E69": [-0.04595, 0.01202, 1, 0, 0.00391], "E71": [-0.04595, -0.00793, 1, 0, 0.00391], "E72": [-0.04617, -0.01778, 1, 0, 0.00443], "E73": [-0.04612, -0.02746, 1, 0, 0.00435], "E74": [-0.04732, -0.03796, 1, 0, 0.00365], "E75": [-0.04597, 0.00224, 1, 0, 0.00391]};
            skSetInitialGuess(sketch, initialGuessF17);
            skSolve(sketch);
        }
        {
            var Q0;
            Q0 = qSketchRegion(id + "F17", true);
            extrude(context, id + "F18", {"entities" : qUnion([Q0]), "operationType" : NewBodyOperationType.REMOVE, "oppositeDirection" : true, "depth" : 3 * mm});
        }
        {
            var Q0;
            Q0=makeQuery(id+"F1.opExtrude","CAP_FACE",FACE,{"disambiguationData":[OSD([sQuery(id+"F0.wireOp",EDGE,"E44.bottom"),sQuery(id+"F0.wireOp",EDGE,"E44.top"),sQuery(id+"F0.wireOp",EDGE,"E44.left"),sQuery(id+"F0.wireOp",EDGE,"E44.right")])],"isStart":false});
            var sketch = newSketch(context, id + "F19", { "sketchPlane" : qUnion([Q0])});
            skText(sketch, "E76", { "text": "3", "fontName": "OpenSans-Regular.ttf"});
            skText(sketch, "E77", { "text": "1", "fontName": "OpenSans-Regular.ttf"});
            skText(sketch, "E78", { "text": "5", "fontName": "OpenSans-Regular.ttf"});
            skText(sketch, "E79", { "text": "7", "fontName": "OpenSans-Regular.ttf"});
            skText(sketch, "E80", { "text": "9", "fontName": "OpenSans-Regular.ttf"});
            skLineSegment(sketch, "E81", {"start": v(-53.42, 42.7) * mm, "end": v(81.58, 42.7) * mm});
            const initialGuessF19  = {"E76": [-0.01806, 0.0427, 1, 0, 0.00598], "E77": [-0.0394, 0.0427, 1, 0, 0.00613], "E78": [0.0059, 0.0427, 1, 0, 0.00614], "E79": [0.03179, 0.0427, 1, 0, 0.00614], "E80": [0.05972, 0.0427, 1, 0, 0.00614]};
            skSetInitialGuess(sketch, initialGuessF19);
            skSolve(sketch);
        }
        {
            var Q0;
            Q0 = qSketchRegion(id + "F19", true);
            extrude(context, id + "F20", {"entities" : qUnion([Q0]), "operationType" : NewBodyOperationType.REMOVE, "oppositeDirection" : true, "depth" : 2 * mm});
        }
        {
            var Q0;
            Q0=makeQuery(id+"F0.imprint","IMPRINT",FACE,{"disambiguationData":[TD([[makeQuery(id+"F0.imprint","IMPRINT",EDGE,{"derivedFrom":sQuery(id+"F0.wireOp",EDGE,"E9.bottom")}),-1.0]])]});
            var Q1;
            Q1=makeQuery(id+"F0.imprint","IMPRINT",FACE,{"disambiguationData":[TD([[makeQuery(id+"F0.imprint","IMPRINT",EDGE,{"derivedFrom":sQuery(id+"F0.wireOp",EDGE,"E27.bottom")}),-1.0]])]});
            extrude(context, id + "F21", {"entities" : qUnion([Q0, Q1]), "operationType" : NewBodyOperationType.ADD, "depth" : 12 * mm});
        }
    });
